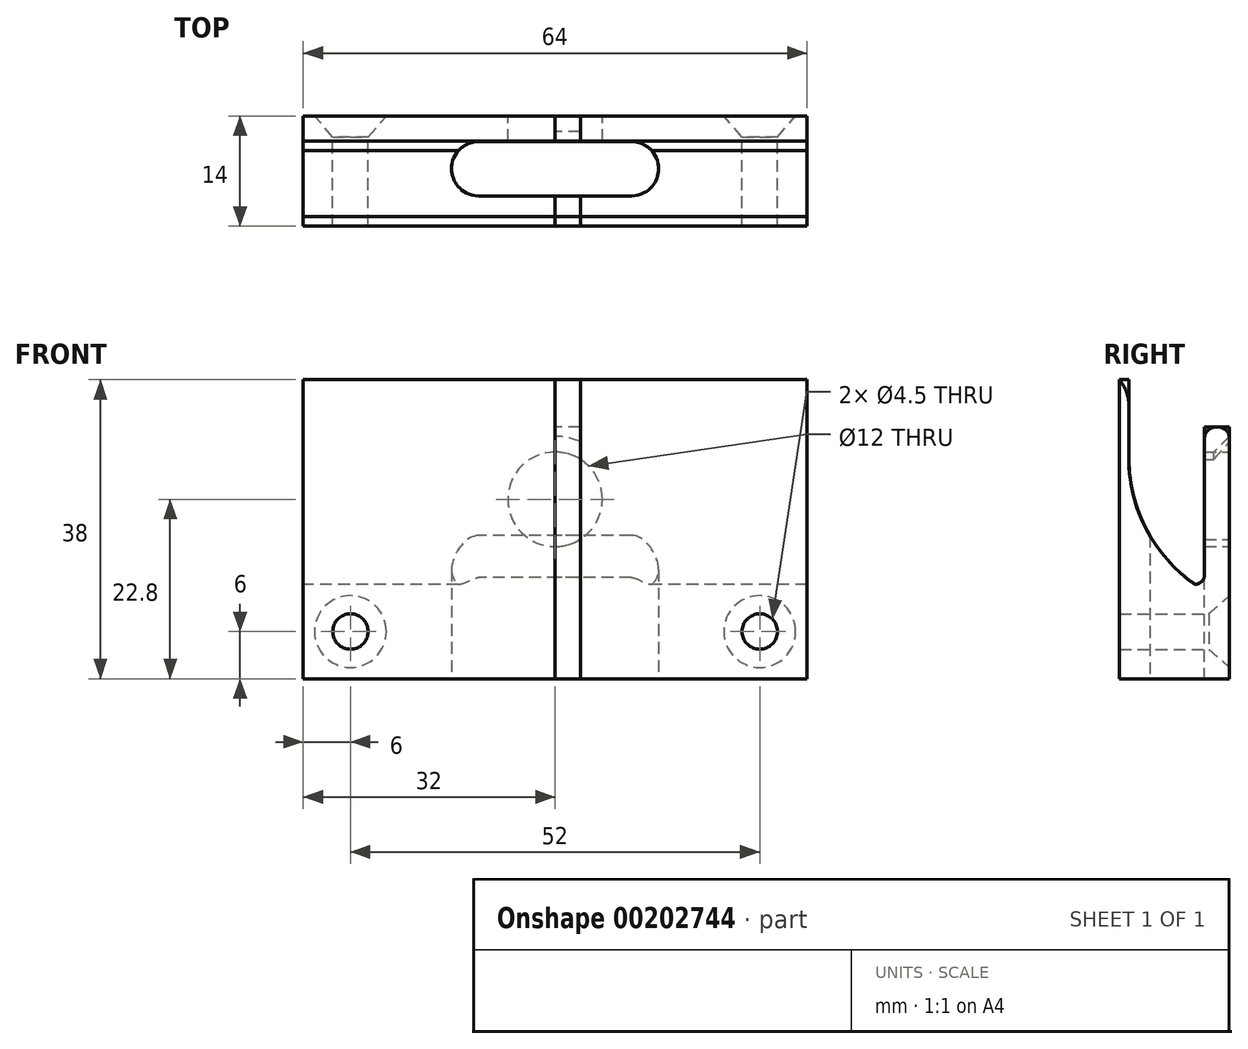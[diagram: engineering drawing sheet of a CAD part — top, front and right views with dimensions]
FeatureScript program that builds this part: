
annotation { "Feature Type Name" : "Feature", "Feature Type Description" : "" }
export const myFeature = defineFeature(function(context is Context, id is Id, definition is map)
    precondition{}
    {
        {
            var Q0;
            Q0=qCreatedBy(makeId("Right.planeOp"),FACE);
            var sketch = newSketch(context, id + "F0", { "sketchPlane" : qUnion([Q0])});
            skLineSegment(sketch, "E0", {"start": v(1.2, 38) * mm, "end": v(1.2, 28) * mm});
            skLineSegment(sketch, "E1", {"start": v(10.8, 32) * mm, "end": v(10.8, 13.2) * mm});
            skArc(sketch, "E2", {"start": v(1.2, 28) * mm, "mid": v(3.43, 18.96) * mm, "end": v(9.6, 12) * mm});
            skArc(sketch, "E3", {"start": v(10.8, 13.2) * mm, "mid": v(10.45, 12.35) * mm, "end": v(9.6, 12) * mm});
            skLineSegment(sketch, "E4", {"start": v(1.2, 38) * mm, "end": v(0, 38) * mm});
            skLineSegment(sketch, "E5", {"start": v(0, 38) * mm, "end": v(0, 0) * mm});
            skLineSegment(sketch, "E6", {"start": v(0, 0) * mm, "end": v(14, 0) * mm});
            skLineSegment(sketch, "E7", {"start": v(14, 0) * mm, "end": v(14, 32) * mm});
            skLineSegment(sketch, "E8", {"start": v(14, 32) * mm, "end": v(10.8, 32) * mm});
            skPoint(sketch, "E9", {"position": v(14, 22.8) * mm});
            skSolve(sketch);
        }
        {
            var Q0;
            Q0=makeQuery(id+"F0.imprint","IMPRINT",FACE,{"disambiguationData":[TD([[makeQuery(id+"F0.imprint","IMPRINT",EDGE,{"derivedFrom":sQuery(id+"F0.wireOp",EDGE,"E0")}),-1.0]])]});
            extrude(context, id + "F1", {"entities" : qUnion([Q0]), "depth" : 3.2 * mm});
        }
        {
            var Q0;
            Q0=makeQuery(id+"F0.imprint","IMPRINT",FACE,{"disambiguationData":[TD([[makeQuery(id+"F0.imprint","IMPRINT",EDGE,{"derivedFrom":sQuery(id+"F0.wireOp",EDGE,"E0")}),-1.0]])]});
            extrude(context, id + "F2", {"entities" : qUnion([Q0]), "endBound" : BoundingType.SYMMETRIC, "depth" : 64 * mm});
        }
        {
            var Q0;
            Q0=qCreatedBy(makeId("Top.planeOp"),FACE);
            var sketch = newSketch(context, id + "F3", { "sketchPlane" : qUnion([Q0])});
            skLineSegment(sketch, "E10.bottom", {"start": v(9.7, 10.75) * mm, "end": v(-9.7, 10.75) * mm});
            skLineSegment(sketch, "E10.top", {"start": v(9.7, 3.85) * mm, "end": v(-9.7, 3.85) * mm});
            skLineSegment(sketch, "E10.left", {"start": v(13.15, 7.3) * mm, "end": v(13.15, 7.3) * mm});
            skLineSegment(sketch, "E10.right", {"start": v(-13.15, 7.3) * mm, "end": v(-13.15, 7.3) * mm});
            skPoint(sketch, "E10.middle", {"position": v(0, 7.3) * mm});
            skPoint(sketch, "E11.visualSharp", {"position": v(-13.15, 3.85) * mm});
            skArc(sketch, "E11.filletArc", {"start": v(-13.15, 7.3) * mm, "mid": v(-12.14, 4.86) * mm, "end": v(-9.7, 3.85) * mm});
            skPoint(sketch, "E12.visualSharp", {"position": v(-13.15, 10.75) * mm});
            skArc(sketch, "E12.filletArc", {"start": v(-9.7, 10.75) * mm, "mid": v(-12.14, 9.74) * mm, "end": v(-13.15, 7.3) * mm});
            skPoint(sketch, "E13.visualSharp", {"position": v(13.15, 3.85) * mm});
            skArc(sketch, "E13.filletArc", {"start": v(9.7, 3.85) * mm, "mid": v(12.14, 4.86) * mm, "end": v(13.15, 7.3) * mm});
            skPoint(sketch, "E14.visualSharp", {"position": v(13.15, 10.75) * mm});
            skArc(sketch, "E14.filletArc", {"start": v(13.15, 7.3) * mm, "mid": v(12.14, 9.74) * mm, "end": v(9.7, 10.75) * mm});
            skSolve(sketch);
        }
        {
            var Q0;
            Q0=makeQuery(id+"F3.imprint","IMPRINT",FACE,{"disambiguationData":[TD([[makeQuery(id+"F3.imprint","IMPRINT",EDGE,{"derivedFrom":sQuery(id+"F3.wireOp",EDGE,"E10.bottom")}),1.0]])]});
            extrude(context, id + "F4", {"entities" : qUnion([Q0]), "operationType" : NewBodyOperationType.REMOVE, "endBound" : BoundingType.THROUGH_ALL, "depth" : 25 * mm});
        }
        {
            var Q0;
            Q0=makeQuery(id+"F2.opExtrude","SWEPT_FACE",FACE,{"disambiguationData":[OSD([sQuery(id+"F0.wireOp",EDGE,"E7")])]});
            var sketch = newSketch(context, id + "F5", { "sketchPlane" : qUnion([Q0])});
            skCircle(sketch, "E15", {"center": v(0, 22.8) * mm, "radius": 6 * mm});
            skPoint(sketch, "E16", {"position": v(-26, 6) * mm});
            skPoint(sketch, "E17", {"position": v(26, 6) * mm});
            skLineSegment(sketch, "E18", {"start": v(-26, 6) * mm, "end": v(26, 6) * mm, "construction": true});
            skPoint(sketch, "E19", {"position": v(0, 6) * mm});
            skSolve(sketch);
        }
        {
            var Q0;
            Q0=makeQuery(id+"F5.imprint","IMPRINT",FACE,{"disambiguationData":[TD([[makeQuery(id+"F5.imprint","IMPRINT",EDGE,{"derivedFrom":sQuery(id+"F5.wireOp",EDGE,"E15")}),1.0]])]});
            var Q1;
            Q1=makeQuery(id+"F2.opExtrude","SWEPT_FACE",FACE,{"disambiguationData":[OSD([sQuery(id+"F0.wireOp",EDGE,"E1")])]});
            extrude(context, id + "F6", {"entities" : qUnion([Q0]), "operationType" : NewBodyOperationType.REMOVE, "endBound" : BoundingType.UP_TO_SURFACE, "oppositeDirection" : true, "endBoundEntityFace" : qUnion([Q1]), "depth" : 25 * mm});
        }
        {
            var Q0;
            Q0=makeQuery(id+"F6.boolean.opBoolean","COPY",EDGE,{"derivedFrom":makeQuery(id+"F6.opExtrude","CAP_EDGE",EDGE,{"disambiguationData":[OSD([sQuery(id+"F5.wireOp",EDGE,"E15")])],"isStart":true})});
            chamfer(context, id + "F7", {"entities" : qUnion([Q0]), "width" : 2 * mm, "tangentPropagation" : true});
        }
        {
            var Q0;
            Q0=makeQuery(id+"F2.opExtrude","SWEPT_EDGE",EDGE,{"disambiguationData":[OSD([sQuery(id+"F0.wireOp",EDGE,"E7"),sQuery(id+"F0.wireOp",EDGE,"E8")])]});
            var Q1;
            Q1=makeQuery(id+"F2.opExtrude","SWEPT_EDGE",EDGE,{"disambiguationData":[OSD([sQuery(id+"F0.wireOp",EDGE,"E1"),sQuery(id+"F0.wireOp",EDGE,"E8")])]});
            fillet(context, id + "F8", {"entities" : qUnion([Q0, Q1]), "radius" : 1.5 * mm, "tangentPropagation" : true, "allowEdgeOverflow" : false});
        }
        {
            var Q0;
            Q0=sQuery(id+"F5.wireOp",VERTEX,"E16");
            var Q1;
            Q1=sQuery(id+"F5.wireOp",VERTEX,"E17");
            var Q2;
            Q2=makeQuery(id+"F2.opExtrude","SWEPT_BODY",BODY,{"disambiguationData":[OSD([sQuery(id+"F0.wireOp",EDGE,"E0"),sQuery(id+"F0.wireOp",EDGE,"E1"),sQuery(id+"F0.wireOp",EDGE,"E2"),sQuery(id+"F0.wireOp",EDGE,"E3"),sQuery(id+"F0.wireOp",EDGE,"E4"),sQuery(id+"F0.wireOp",EDGE,"E5"),sQuery(id+"F0.wireOp",EDGE,"E6"),sQuery(id+"F0.wireOp",EDGE,"E7"),sQuery(id+"F0.wireOp",EDGE,"E8")])]});
            hole(context, id + "F9", {"style" : HoleStyle.C_SINK, "endStyle" : HoleEndStyle.THROUGH, "standardTappedOrClearance" : lookupTablePath({ "standard" : "ANSI", "fit" : "Normal (ASME)", "size" : "#8", "type" : "Clearance" }), "standardBlindInLast" : lookupTablePath({ "fit" : "Free", "standard" : "ANSI", "size" : "#8", "type" : "Clearance" }), "holeDiameter" : 4.5 * mm, "cSinkDiameter" : 9.12 * mm, "cSinkAngle" : 82 * degree, "locations" : qUnion([Q0, Q1]), "scope" : qUnion([Q2]), "isTappedThrough" : true});
        }
        {
            var Q0;
            Q0=makeQuery(id+"F2.opExtrude","SWEPT_EDGE",EDGE,{"disambiguationData":[OSD([sQuery(id+"F0.wireOp",EDGE,"E0"),sQuery(id+"F0.wireOp",EDGE,"E4")])]});
            fillet(context, id + "F10", {"entities" : qUnion([Q0]), "radius" : 5 * mm, "tangentPropagation" : true, "allowEdgeOverflow" : false});
        }
    });
